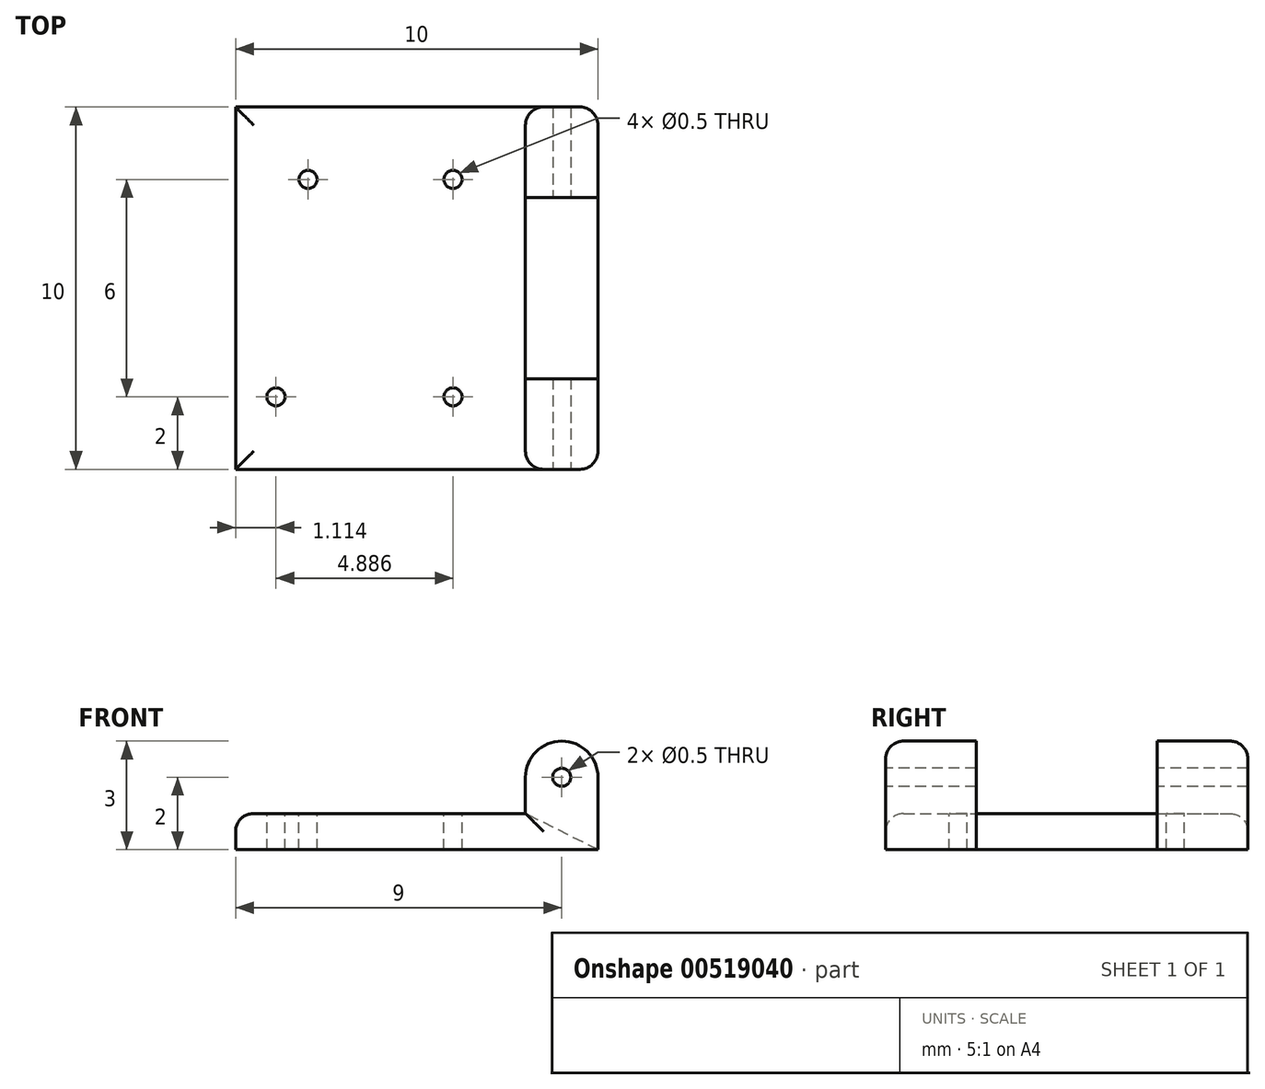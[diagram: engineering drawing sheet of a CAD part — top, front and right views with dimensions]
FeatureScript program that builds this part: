
annotation { "Feature Type Name" : "Feature", "Feature Type Description" : "" }
export const myFeature = defineFeature(function(context is Context, id is Id, definition is map)
    precondition{}
    {
        {
            var Q0;
            Q0=qCreatedBy(makeId("Front.planeOp"),FACE);
            var sketch = newSketch(context, id + "F0", { "sketchPlane" : qUnion([Q0])});
            skLineSegment(sketch, "E0.bottom", {"start": v(0, 0) * mm, "end": v(-10, 0) * mm});
            skLineSegment(sketch, "E0.top", {"start": v(0, 1) * mm, "end": v(-10, 1) * mm});
            skLineSegment(sketch, "E0.left", {"start": v(0, 0) * mm, "end": v(0, 1) * mm});
            skLineSegment(sketch, "E0.right", {"start": v(-10, 0) * mm, "end": v(-10, 1) * mm});
            skCircle(sketch, "E1", {"center": v(-1, 2) * mm, "radius": 1 * mm});
            skLineSegment(sketch, "E2", {"start": v(-2, 2) * mm, "end": v(-2, 1) * mm});
            skLineSegment(sketch, "E3", {"start": v(0, 2) * mm, "end": v(0, 1) * mm});
            skSolve(sketch);
        }
        {
            var Q0;
            Q0 = qSketchRegion(id + "F0", true);
            extrude(context, id + "F1", {"entities" : qUnion([Q0]), "depth" : 10 * mm, "offsetDistance" : 25 * mm});
        }
        {
            var Q0;
            Q0=makeQuery(id+"F1.opExtrude","SWEPT_FACE",FACE,{"disambiguationData":[OSD([sQuery(id+"F0.wireOp",EDGE,"E0.top")])]});
            var sketch = newSketch(context, id + "F2", { "sketchPlane" : qUnion([Q0])});
            skPoint(sketch, "E4", {"position": v(-8.89, -8) * mm});
            skPoint(sketch, "E5", {"position": v(-4, -8) * mm});
            skPoint(sketch, "E6", {"position": v(-4, -2) * mm});
            skPoint(sketch, "E7", {"position": v(-8, -2) * mm});
            skSolve(sketch);
        }
        {
            var Q0;
            Q0=sQuery(id+"F2.wireOp",VERTEX,"E7");
            var Q1;
            Q1=sQuery(id+"F2.wireOp",VERTEX,"E4");
            var Q2;
            Q2=sQuery(id+"F2.wireOp",VERTEX,"E5");
            var Q3;
            Q3=sQuery(id+"F2.wireOp",VERTEX,"E6");
            var Q4;
            Q4=makeQuery(id+"F1.opExtrude","SWEPT_BODY",BODY,{"disambiguationData":[OSD([sQuery(id+"F0.wireOp",EDGE,"E0.bottom"),sQuery(id+"F0.wireOp",EDGE,"E0.top"),sQuery(id+"F0.wireOp",EDGE,"E0.left"),sQuery(id+"F0.wireOp",EDGE,"E0.right"),sQuery(id+"F0.wireOp",EDGE,"E1"),sQuery(id+"F0.wireOp",EDGE,"E2"),sQuery(id+"F0.wireOp",EDGE,"E3")])]});
            hole(context, id + "F3", {"style" : HoleStyle.SIMPLE, "endStyle" : HoleEndStyle.THROUGH, "standardTappedOrClearance" : lookupTablePath({ "standard" : "Custom", "fit" : "Normal", "size" : "M3", "type" : "Clearance" }), "standardBlindInLast" : lookupTablePath({ "fit" : "Standard", "standard" : "Custom", "size" : "M3", "type" : "Clearance" }), "holeDiameter" : .5 * mm, "isTappedThrough" : true, "tappedDepth" : 12 * mm, "tapClearance" : 3, "locations" : qUnion([Q0, Q1, Q2, Q3]), "scope" : qUnion([Q4])});
        }
        {
            var Q0;
            Q0=makeQuery(id+"F1.opExtrude","CAP_FACE",FACE,{"disambiguationData":[OSD([sQuery(id+"F0.wireOp",EDGE,"E0.bottom"),sQuery(id+"F0.wireOp",EDGE,"E0.top"),sQuery(id+"F0.wireOp",EDGE,"E0.left"),sQuery(id+"F0.wireOp",EDGE,"E0.right"),sQuery(id+"F0.wireOp",EDGE,"E1"),sQuery(id+"F0.wireOp",EDGE,"E2"),sQuery(id+"F0.wireOp",EDGE,"E3")])],"isStart":false});
            var sketch = newSketch(context, id + "F4", { "sketchPlane" : qUnion([Q0])});
            skPoint(sketch, "E8", {"position": v(-1, 2) * mm});
            skSolve(sketch);
        }
        {
            var Q0;
            Q0=sQuery(id+"F4.wireOp",VERTEX,"E8");
            var Q1;
            Q1=makeQuery(id+"F1.opExtrude","SWEPT_BODY",BODY,{"disambiguationData":[OSD([sQuery(id+"F0.wireOp",EDGE,"E0.bottom"),sQuery(id+"F0.wireOp",EDGE,"E0.top"),sQuery(id+"F0.wireOp",EDGE,"E0.left"),sQuery(id+"F0.wireOp",EDGE,"E0.right"),sQuery(id+"F0.wireOp",EDGE,"E1"),sQuery(id+"F0.wireOp",EDGE,"E2"),sQuery(id+"F0.wireOp",EDGE,"E3")])]});
            hole(context, id + "F5", {"style" : HoleStyle.SIMPLE, "endStyle" : HoleEndStyle.THROUGH, "holeDiameter" : 0.5 * mm, "isTappedThrough" : true, "tappedDepth" : 12 * mm, "tapClearance" : 3, "locations" : qUnion([Q0]), "scope" : qUnion([Q1])});
        }
        {
            var Q0;
            Q0=makeQuery(id+"F1.opExtrude","CAP_FACE",FACE,{"disambiguationData":[OSD([sQuery(id+"F0.wireOp",EDGE,"E0.bottom"),sQuery(id+"F0.wireOp",EDGE,"E0.top"),sQuery(id+"F0.wireOp",EDGE,"E0.left"),sQuery(id+"F0.wireOp",EDGE,"E0.right"),sQuery(id+"F0.wireOp",EDGE,"E1"),sQuery(id+"F0.wireOp",EDGE,"E2"),sQuery(id+"F0.wireOp",EDGE,"E3")])],"isStart":false});
            cPlane(context, id + "F6", {"entities" : qUnion([Q0]), "cplaneType" : CPlaneType.OFFSET, "offset" : 2.5 * mm, "oppositeDirection" : true, "width" : 150 * mm, "height" : 150 * mm});
        }
        {
            var Q0;
            Q0=qCreatedBy(id+"F6.planeOp",FACE);
            var sketch = newSketch(context, id + "F7", { "sketchPlane" : qUnion([Q0])});
            skCircle(sketch, "E9", {"center": v(-1, 2) * mm, "radius": 1 * mm});
            skLineSegment(sketch, "E10", {"start": v(0, 0) * mm, "end": v(0, 2) * mm});
            skLineSegment(sketch, "E11", {"start": v(0, 0) * mm, "end": v(-2, 1) * mm});
            skLineSegment(sketch, "E12", {"start": v(-2, 1) * mm, "end": v(-2, 2) * mm});
            skSolve(sketch);
        }
        {
            var Q0;
            Q0 = qSketchRegion(id + "F7", true);
            extrude(context, id + "F8", {"entities" : qUnion([Q0]), "operationType" : NewBodyOperationType.REMOVE, "oppositeDirection" : true, "depth" : 5 * mm, "offsetDistance" : 25 * mm});
        }
        {
            var Q0;
            Q0=makeQuery(id+"F1.opExtrude","SWEPT_EDGE",EDGE,{"disambiguationData":[OSD([sQuery(id+"F0.wireOp",EDGE,"E0.top"),sQuery(id+"F0.wireOp",EDGE,"E0.right")])]});
            var Q1;
            Q1=makeQuery(id+"F1.opExtrude","CAP_EDGE",EDGE,{"disambiguationData":[OSD([sQuery(id+"F0.wireOp",EDGE,"E0.top")])],"isStart":false});
            var Q2;
            Q2=makeQuery(id+"F1.opExtrude","CAP_EDGE",EDGE,{"disambiguationData":[OSD([sQuery(id+"F0.wireOp",EDGE,"E0.top")])],"isStart":true});
            fillet(context, id + "F9", {"entities" : qUnion([Q0, Q1, Q2]), "radius" : 0.5 * mm, "tangentPropagation" : true, "allowEdgeOverflow" : false});
        }
        {
            var Q0;
            Q0=makeQuery(id+"F1.opExtrude","CAP_EDGE",EDGE,{"disambiguationData":[OSD([sQuery(id+"F0.wireOp",EDGE,"E0.left"),sQuery(id+"F0.wireOp",EDGE,"E3")])],"isStart":false});
            var Q1;
            Q1=makeQuery(id+"F1.opExtrude","CAP_EDGE",EDGE,{"disambiguationData":[OSD([sQuery(id+"F0.wireOp",EDGE,"E1")])],"isStart":false});
            var Q2;
            Q2=makeQuery(id+"F1.opExtrude","CAP_EDGE",EDGE,{"disambiguationData":[OSD([sQuery(id+"F0.wireOp",EDGE,"E2")])],"isStart":false});
            fillet(context, id + "F10", {"entities" : qUnion([Q0, Q1, Q2]), "radius" : 0.5 * mm, "tangentPropagation" : true, "allowEdgeOverflow" : false});
        }
        {
            var Q0;
            Q0=makeQuery(id+"F1.opExtrude","CAP_EDGE",EDGE,{"disambiguationData":[OSD([sQuery(id+"F0.wireOp",EDGE,"E2")])],"isStart":true});
            var Q1;
            Q1=makeQuery(id+"F1.opExtrude","CAP_EDGE",EDGE,{"disambiguationData":[OSD([sQuery(id+"F0.wireOp",EDGE,"E0.left"),sQuery(id+"F0.wireOp",EDGE,"E3")])],"isStart":true});
            var Q2;
            Q2=makeQuery(id+"F1.opExtrude","CAP_EDGE",EDGE,{"disambiguationData":[OSD([sQuery(id+"F0.wireOp",EDGE,"E1")])],"isStart":true});
            fillet(context, id + "F11", {"entities" : qUnion([Q0, Q1, Q2]), "radius" : 0.5 * mm, "tangentPropagation" : true, "allowEdgeOverflow" : false});
        }
    });
